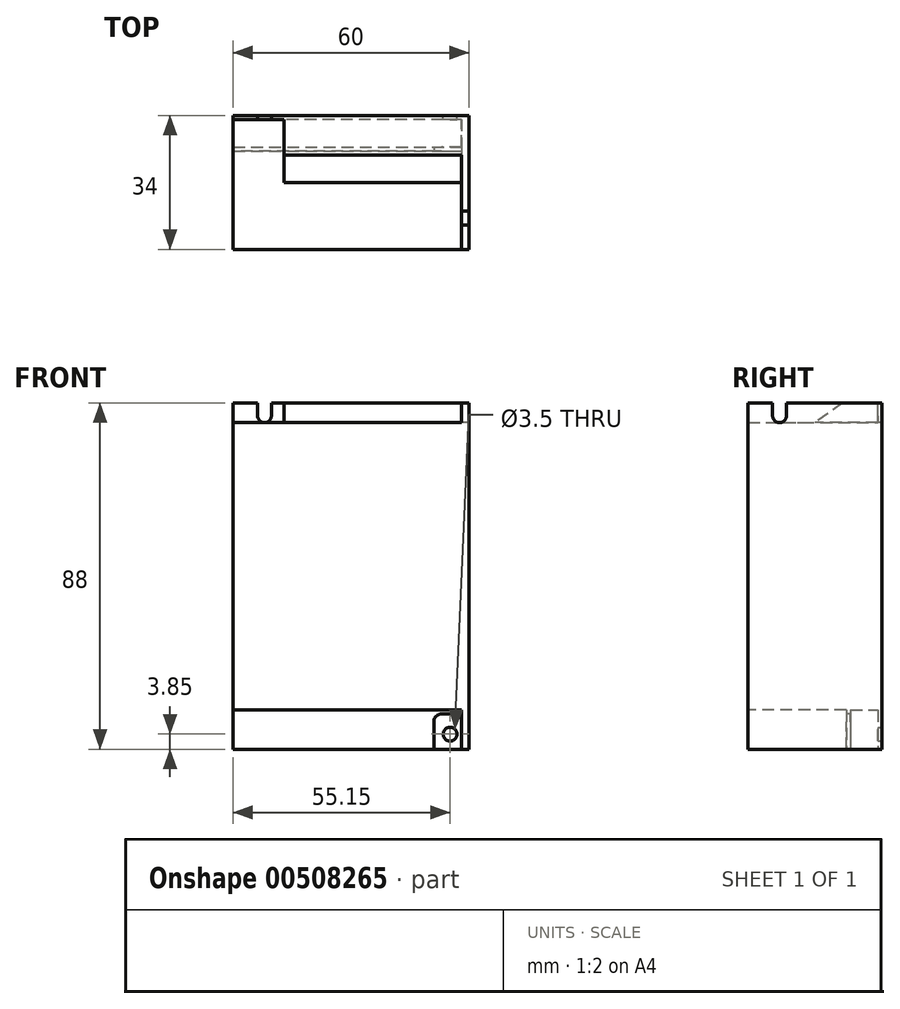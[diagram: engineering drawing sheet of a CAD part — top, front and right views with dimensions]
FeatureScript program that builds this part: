
annotation { "Feature Type Name" : "Feature", "Feature Type Description" : "" }
export const myFeature = defineFeature(function(context is Context, id is Id, definition is map)
    precondition{}
    {
        {
            var Q0;
            Q0=qCreatedBy(makeId("Front.planeOp"),FACE);
            var sketch = newSketch(context, id + "F0", { "sketchPlane" : qUnion([Q0])});
            skLineSegment(sketch, "E0.bottom", {"start": v(30, 44) * mm, "end": v(-30, 44) * mm});
            skLineSegment(sketch, "E0.top", {"start": v(30, -44) * mm, "end": v(-30, -44) * mm});
            skLineSegment(sketch, "E0.left", {"start": v(30, 44) * mm, "end": v(30, -44) * mm});
            skLineSegment(sketch, "E0.right", {"start": v(-30, 44) * mm, "end": v(-30, -44) * mm});
            skPoint(sketch, "E0.middle", {"position": v(0, 0) * mm});
            skSolve(sketch);
        }
        {
            var Q0;
            Q0=makeQuery(id+"F0.imprint","IMPRINT",FACE,{"disambiguationData":[TD([[makeQuery(id+"F0.imprint","IMPRINT",EDGE,{"derivedFrom":sQuery(id+"F0.wireOp",EDGE,"E0.bottom")}),1.0]])]});
            extrude(context, id + "F1", {"entities" : qUnion([Q0]), "depth" : 34 * mm});
        }
        {
            var Q0;
            Q0=makeQuery(id+"F1.opExtrude","SWEPT_FACE",FACE,{"disambiguationData":[OSD([sQuery(id+"F0.wireOp",EDGE,"E0.right")])]});
            var sketch = newSketch(context, id + "F2", { "sketchPlane" : qUnion([Q0])});
            skLineSegment(sketch, "E1", {"start": v(34, 44) * mm, "end": v(34, 39) * mm});
            skLineSegment(sketch, "E2", {"start": v(34, 39) * mm, "end": v(17, 39) * mm});
            skLineSegment(sketch, "E3", {"start": v(17, 39) * mm, "end": v(10, 44) * mm});
            skSolve(sketch);
        }
        {
            var Q0;
            {var subQ0=sQuery(id+"F2.wireOp",EDGE,"E1");Q0=makeQuery(id+"F2.imprint","IMPRINT",FACE,{"disambiguationData":[TD([[makeQuery(id+"F2.imprint","IMPRINT",EDGE,{"derivedFrom":subQ0}),-1.0]])]});}
            extrude(context, id + "F3", {"entities" : qUnion([Q0]), "operationType" : NewBodyOperationType.REMOVE, "oppositeDirection" : true, "depth" : 58 * mm});
        }
        {
            var Q0;
            Q0=makeQuery(id+"F1.opExtrude","CAP_FACE",FACE,{"disambiguationData":[OSD([sQuery(id+"F0.wireOp",EDGE,"E0.bottom"),sQuery(id+"F0.wireOp",EDGE,"E0.top"),sQuery(id+"F0.wireOp",EDGE,"E0.left"),sQuery(id+"F0.wireOp",EDGE,"E0.right")])],"isStart":false});
            var sketch = newSketch(context, id + "F4", { "sketchPlane" : qUnion([Q0])});
            skLineSegment(sketch, "E4.0", {"start": v(28, 44) * mm, "end": v(-30, 44) * mm});
            skLineSegment(sketch, "E5.0", {"start": v(-30, 39) * mm, "end": v(-30, 44) * mm});
            skLineSegment(sketch, "E6", {"start": v(-30, 44) * mm, "end": v(-17, 44) * mm});
            skLineSegment(sketch, "E7", {"start": v(-17, 44) * mm, "end": v(-17, 39) * mm});
            skLineSegment(sketch, "E8", {"start": v(-30, -34) * mm, "end": v(28, -34) * mm});
            skLineSegment(sketch, "E9", {"start": v(28, -34) * mm, "end": v(28, -44) * mm});
            skSolve(sketch);
        }
        {
            var Q0;
            {var subQ0=sQuery(id+"F4.wireOp",EDGE,"E5.0");Q0=makeQuery(id+"F4.imprint","IMPRINT",FACE,{"disambiguationData":[TD([[makeQuery(id+"F4.imprint","IMPRINT",EDGE,{"derivedFrom":subQ0}),-1.0]])]});}
            extrude(context, id + "F5", {"entities" : qUnion([Q0]), "operationType" : NewBodyOperationType.REMOVE, "oppositeDirection" : true, "depth" : 33 * mm});
        }
        {
            var Q0;
            Q0=makeQuery(id+"F5.boolean.opBoolean","COPY",FACE,{"derivedFrom":makeQuery(id+"F5.opExtrude","CAP_FACE",FACE,{"disambiguationData":[OSD([sQuery(id+"F0.wireOp",EDGE,"E0.right"),sQuery(id+"F2.wireOp",EDGE,"E1"),sQuery(id+"F2.wireOp",EDGE,"E2"),sQuery(id+"F4.wireOp",EDGE,"E5.0"),sQuery(id+"F4.wireOp",EDGE,"E6"),sQuery(id+"F4.wireOp",EDGE,"E7")])],"isStart":false})});
            var sketch = newSketch(context, id + "F6", { "sketchPlane" : qUnion([Q0])});
            skArc(sketch, "E10", {"start": v(-23.75, 40.7) * mm, "mid": v(-21.98, 39) * mm, "end": v(-20.25, 40.75) * mm});
            skLineSegment(sketch, "E11", {"start": v(-23.75, 40.7) * mm, "end": v(-23.83, 44) * mm});
            skLineSegment(sketch, "E12", {"start": v(-20.25, 40.75) * mm, "end": v(-20.25, 44) * mm});
            skSolve(sketch);
        }
        {
            var Q0;
            {var subQ1=sQuery(id+"F6.wireOp",EDGE,"E11");Q0=makeQuery(id+"F6.imprint","IMPRINT",FACE,{"disambiguationData":[TD([[makeQuery(id+"F6.imprint","IMPRINT",EDGE,{"derivedFrom":subQ1}),-1.0]])]});}
            extrude(context, id + "F7", {"entities" : qUnion([Q0]), "operationType" : NewBodyOperationType.REMOVE, "endBound" : BoundingType.THROUGH_ALL, "oppositeDirection" : true, "depth" : 25 * mm});
        }
        {
            var Q0;
            Q0=makeQuery(id+"F3.boolean.opBoolean","COPY",FACE,{"derivedFrom":makeQuery(id+"F3.opExtrude","CAP_FACE",FACE,{"disambiguationData":[OSD([sQuery(id+"F0.wireOp",EDGE,"E0.bottom"),sQuery(id+"F0.wireOp",EDGE,"E0.right"),sQuery(id+"F2.wireOp",EDGE,"E1"),sQuery(id+"F2.wireOp",EDGE,"E2"),sQuery(id+"F2.wireOp",EDGE,"E3")])],"isStart":false})});
            var sketch = newSketch(context, id + "F8", { "sketchPlane" : qUnion([Q0])});
            skArc(sketch, "E13", {"start": v(24.25, 40.75) * mm, "mid": v(26, 39) * mm, "end": v(27.75, 40.75) * mm});
            skLineSegment(sketch, "E14", {"start": v(27.75, 40.75) * mm, "end": v(27.75, 44) * mm});
            skLineSegment(sketch, "E15", {"start": v(24.25, 40.75) * mm, "end": v(24.25, 44) * mm});
            skSolve(sketch);
        }
        {
            var Q0;
            {var subQ1=sQuery(id+"F8.wireOp",EDGE,"E14");Q0=makeQuery(id+"F8.imprint","IMPRINT",FACE,{"disambiguationData":[TD([[makeQuery(id+"F8.imprint","IMPRINT",EDGE,{"derivedFrom":subQ1}),1.0]])]});}
            extrude(context, id + "F9", {"entities" : qUnion([Q0]), "operationType" : NewBodyOperationType.REMOVE, "endBound" : BoundingType.THROUGH_ALL, "oppositeDirection" : true, "depth" : 25 * mm});
        }
        {
            var Q0;
            {var subQ0=sQuery(id+"F4.wireOp",EDGE,"E8");Q0=makeQuery(id+"F4.imprint","IMPRINT",FACE,{"disambiguationData":[TD([[makeQuery(id+"F4.imprint","IMPRINT",EDGE,{"derivedFrom":subQ0}),-1.0]])]});}
            extrude(context, id + "F10", {"entities" : qUnion([Q0]), "operationType" : NewBodyOperationType.REMOVE, "oppositeDirection" : true, "depth" : 25 * mm});
        }
        {
            var Q0;
            Q0=makeQuery(id+"F1.opExtrude","SWEPT_FACE",FACE,{"disambiguationData":[OSD([sQuery(id+"F0.wireOp",EDGE,"E0.top")])]});
            var sketch = newSketch(context, id + "F11", { "sketchPlane" : qUnion([Q0])});
            skLineSegment(sketch, "E16", {"start": v(-30, 8) * mm, "end": v(28, 8) * mm});
            skLineSegment(sketch, "E17", {"start": v(28, 8) * mm, "end": v(28, 1) * mm});
            skLineSegment(sketch, "E18", {"start": v(28, 1) * mm, "end": v(-30, 1) * mm});
            skLineSegment(sketch, "E19", {"start": v(-30, 1) * mm, "end": v(-30, 8) * mm});
            skSolve(sketch);
        }
        {
            var Q0;
            Q0=makeQuery(id+"F11.imprint","IMPRINT",FACE,{"disambiguationData":[TD([[makeQuery(id+"F11.imprint","IMPRINT",EDGE,{"derivedFrom":sQuery(id+"F11.wireOp",EDGE,"E16")}),-1.0]])]});
            extrude(context, id + "F12", {"entities" : qUnion([Q0]), "operationType" : NewBodyOperationType.REMOVE, "oppositeDirection" : true, "depth" : 10 * mm});
        }
        {
            var Q0;
            Q0=makeQuery(id+"F10.boolean.opBoolean","COPY",FACE,{"derivedFrom":makeQuery(id+"F10.opExtrude","CAP_FACE",FACE,{"disambiguationData":[OSD([sQuery(id+"F0.wireOp",EDGE,"E0.top"),sQuery(id+"F0.wireOp",EDGE,"E0.right"),sQuery(id+"F4.wireOp",EDGE,"E8"),sQuery(id+"F4.wireOp",EDGE,"E9")])],"isStart":false})});
            var sketch = newSketch(context, id + "F13", { "sketchPlane" : qUnion([Q0])});
            skLineSegment(sketch, "E20", {"start": v(21, -44) * mm, "end": v(21, -37) * mm});
            skLineSegment(sketch, "E21", {"start": v(23, -35) * mm, "end": v(28, -35) * mm});
            skPoint(sketch, "E22.visualSharp", {"position": v(21, -35) * mm});
            skArc(sketch, "E22.filletArc", {"start": v(23, -35) * mm, "mid": v(21.59, -35.59) * mm, "end": v(21, -37) * mm});
            skSolve(sketch);
        }
        {
            var Q0;
            {var subQ4=sQuery(id+"F13.wireOp",EDGE,"E20");Q0=makeQuery(id+"F13.imprint","IMPRINT",FACE,{"disambiguationData":[TD([[makeQuery(id+"F13.imprint","IMPRINT",EDGE,{"derivedFrom":subQ4}),-1.0]])]});}
            extrude(context, id + "F14", {"entities" : qUnion([Q0]), "operationType" : NewBodyOperationType.REMOVE, "oppositeDirection" : true, "depth" : 3 * mm});
        }
        {
            var Q0;
            Q0=makeQuery(id+"F1.opExtrude","CAP_FACE",FACE,{"disambiguationData":[OSD([sQuery(id+"F0.wireOp",EDGE,"E0.bottom"),sQuery(id+"F0.wireOp",EDGE,"E0.top"),sQuery(id+"F0.wireOp",EDGE,"E0.left"),sQuery(id+"F0.wireOp",EDGE,"E0.right")])],"isStart":true});
            var sketch = newSketch(context, id + "F15", { "sketchPlane" : qUnion([Q0])});
            skCircle(sketch, "E23", {"center": v(-25.15, -40.15) * mm, "radius": 1.75 * mm});
            skSolve(sketch);
        }
        {
            var Q0;
            Q0=makeQuery(id+"F15.imprint","IMPRINT",FACE,{"disambiguationData":[TD([[makeQuery(id+"F15.imprint","IMPRINT",EDGE,{"derivedFrom":sQuery(id+"F15.wireOp",EDGE,"E23")}),1.0]])]});
            extrude(context, id + "F16", {"entities" : qUnion([Q0]), "operationType" : NewBodyOperationType.REMOVE, "oppositeDirection" : true, "depth" : 3 * mm});
        }
    });
